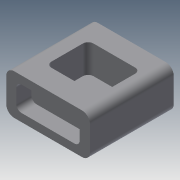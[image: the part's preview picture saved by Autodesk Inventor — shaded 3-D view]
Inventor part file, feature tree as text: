
AUTODESK INVENTOR PART (.ipt)
format: ipt  version: 2015 (Build 190159000, 159)  size: 130,048 bytes
history: native  units: in
note: dims shown in document units (in); Inventor stores cm internally (conversion verified against a paired STEP export)
features: extrude x3, sketch x3
ambient origin geometry x8: Origin, YZ Plane, XZ Plane, XY Plane, X Axis, Y Axis, Z Axis, Center Point
bodies: Solid1 (feature_tree)
feature tree (6):
  extrude  "Extrusion1"  Depth=1.53in
  extrude  "Extrusion2"  Depth=0.3in
  extrude  "Extrusion3"  Depth=0.3in
  sketch  "Sketch1"  dims[d0=3.17in d1=1.53in]
  sketch  "Sketch2"  dims[d2=0.3in d3=0.3in]
  sketch  "Sketch3"  dims[d4=0.3in d5=0.3in d14=3.17in d15=0.0in d16=1.59in d17=1.98in d18=0.82in d19=0.5in d20=0.2in d21=0.2in d22=0.2in d23=0.2in d24=1.07in d25=0.0in d26=2.4in d27=0.39in d28=0.93in d29=0.3in d30=0.2in d31=0.2in d32=0.57in d33=0.0in]
